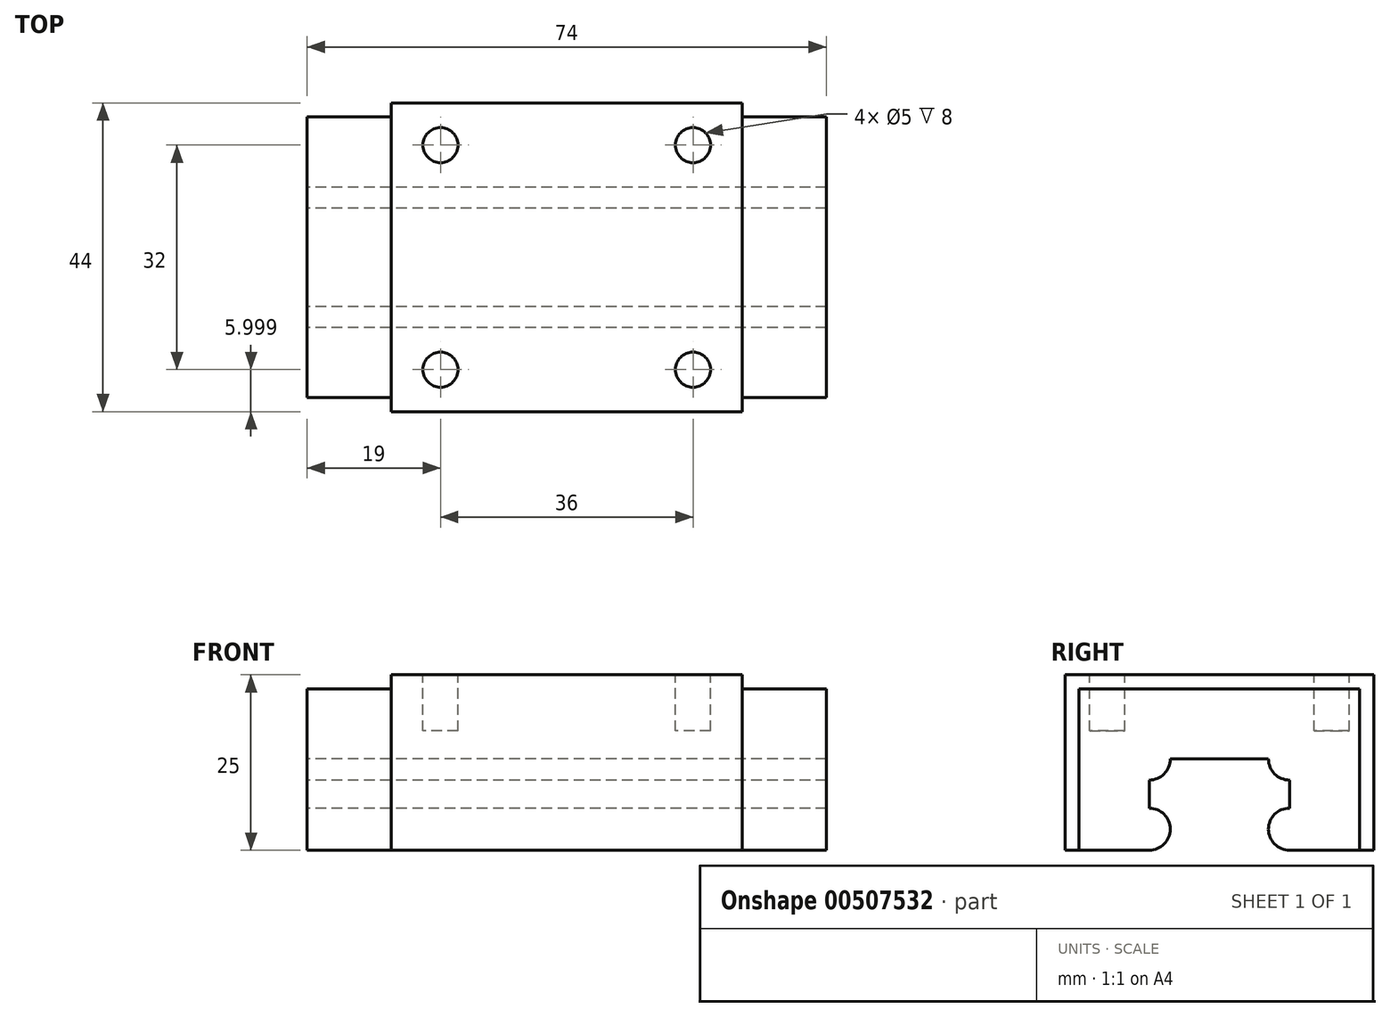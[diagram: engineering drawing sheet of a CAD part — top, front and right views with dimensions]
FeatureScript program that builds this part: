
annotation { "Feature Type Name" : "Feature", "Feature Type Description" : "" }
export const myFeature = defineFeature(function(context is Context, id is Id, definition is map)
    precondition{}
    {
        {
            var Q0;
            Q0=qCreatedBy(makeId("Right.planeOp"),FACE);
            var sketch = newSketch(context, id + "F0", { "sketchPlane" : qUnion([Q0])});
            skLineSegment(sketch, "E0", {"start": v(-26.04, 11) * mm, "end": v(-26.04, 15) * mm});
            skLineSegment(sketch, "E1", {"start": v(-23.04, 18) * mm, "end": v(-9.04, 18) * mm});
            skLineSegment(sketch, "E2", {"start": v(-6.04, 15) * mm, "end": v(-6.04, 11) * mm});
            skArc(sketch, "E3", {"start": v(-26.04, 5) * mm, "mid": v(-23.04, 8) * mm, "end": v(-26.04, 11) * mm});
            skArc(sketch, "E4", {"start": v(-6.04, 11) * mm, "mid": v(-9.04, 8) * mm, "end": v(-6.04, 5) * mm});
            skArc(sketch, "E5", {"start": v(-26.04, 15) * mm, "mid": v(-23.92, 15.88) * mm, "end": v(-23.04, 18) * mm});
            skArc(sketch, "E6", {"start": v(-9.04, 18) * mm, "mid": v(-8.16, 15.88) * mm, "end": v(-6.04, 15) * mm});
            skLineSegment(sketch, "E7", {"start": v(-38.04, 30) * mm, "end": v(5.96, 30) * mm});
            skLineSegment(sketch, "E8", {"start": v(-26.04, 5) * mm, "end": v(-38.04, 5) * mm});
            skLineSegment(sketch, "E9", {"start": v(-6.04, 5) * mm, "end": v(5.96, 5) * mm});
            skLineSegment(sketch, "E10", {"start": v(-38.04, 5) * mm, "end": v(-38.04, 30) * mm});
            skLineSegment(sketch, "E11", {"start": v(5.96, 5) * mm, "end": v(5.96, 30) * mm});
            skSolve(sketch);
        }
        {
            var Q0;
            Q0=qSketchRegion(id+"F0",true);
            extrude(context, id + "F1", {"entities" : qUnion([Q0]), "depth" : 74 * mm});
        }
        {
            var Q0;
            Q0=makeQuery(id+"F1.opExtrude","SWEPT_FACE",FACE,{"disambiguationData":[OSD([sQuery(id+"F0.wireOp",EDGE,"E7")])]});
            var sketch = newSketch(context, id + "F2", { "sketchPlane" : qUnion([Q0])});
            skLineSegment(sketch, "E12.bottom", {"start": v(74, -38.04) * mm, "end": v(62, -38.04) * mm});
            skLineSegment(sketch, "E12.top", {"start": v(74, 5.96) * mm, "end": v(62, 5.96) * mm});
            skLineSegment(sketch, "E12.left", {"start": v(74, -38.04) * mm, "end": v(74, 5.96) * mm});
            skLineSegment(sketch, "E12.right", {"start": v(62, -38.04) * mm, "end": v(62, 5.96) * mm});
            skLineSegment(sketch, "E13.bottom", {"start": v(0, -38.04) * mm, "end": v(12, -38.04) * mm});
            skLineSegment(sketch, "E13.top", {"start": v(0, 5.96) * mm, "end": v(12, 5.96) * mm});
            skLineSegment(sketch, "E13.left", {"start": v(0, -38.04) * mm, "end": v(0, 5.96) * mm});
            skLineSegment(sketch, "E13.right", {"start": v(12, -38.04) * mm, "end": v(12, 5.96) * mm});
            skSolve(sketch);
        }
        {
            var Q0;
            Q0=qSketchRegion(id+"F2",true);
            extrude(context, id + "F3", {"entities" : qUnion([Q0]), "operationType" : NewBodyOperationType.REMOVE, "oppositeDirection" : true, "depth" : 2 * mm});
        }
        {
            var Q0;
            Q0=makeQuery(id+"F1.opExtrude","SWEPT_FACE",FACE,{"disambiguationData":[OSD([sQuery(id+"F0.wireOp",EDGE,"E7")])]});
            var sketch = newSketch(context, id + "F4", { "sketchPlane" : qUnion([Q0])});
            skLineSegment(sketch, "E14.bottom", {"start": v(12, 5.96) * mm, "end": v(0, 5.96) * mm});
            skLineSegment(sketch, "E14.top", {"start": v(12, 3.96) * mm, "end": v(0, 3.96) * mm});
            skLineSegment(sketch, "E14.left", {"start": v(12, 5.96) * mm, "end": v(12, 3.96) * mm});
            skLineSegment(sketch, "E14.right", {"start": v(0, 5.96) * mm, "end": v(0, 3.96) * mm});
            skLineSegment(sketch, "E15.bottom", {"start": v(12, -38.04) * mm, "end": v(0, -38.04) * mm});
            skLineSegment(sketch, "E15.top", {"start": v(12, -36.04) * mm, "end": v(0, -36.04) * mm});
            skLineSegment(sketch, "E15.left", {"start": v(12, -38.04) * mm, "end": v(12, -36.04) * mm});
            skLineSegment(sketch, "E15.right", {"start": v(0, -38.04) * mm, "end": v(0, -36.04) * mm});
            skPoint(sketch, "E16.oppositeSnap0", {"position": v(6, -36.04) * mm});
            skLineSegment(sketch, "E16.bottom", {"start": v(62, -38.04) * mm, "end": v(74, -38.04) * mm});
            skLineSegment(sketch, "E16.top", {"start": v(62, -36.04) * mm, "end": v(74, -36.04) * mm});
            skLineSegment(sketch, "E16.left", {"start": v(62, -38.04) * mm, "end": v(62, -36.04) * mm});
            skLineSegment(sketch, "E16.right", {"start": v(74, -38.04) * mm, "end": v(74, -36.04) * mm});
            skLineSegment(sketch, "E17.bottom", {"start": v(62, 5.96) * mm, "end": v(74, 5.96) * mm});
            skLineSegment(sketch, "E17.top", {"start": v(62, 3.96) * mm, "end": v(74, 3.96) * mm});
            skLineSegment(sketch, "E17.left", {"start": v(62, 5.96) * mm, "end": v(62, 3.96) * mm});
            skLineSegment(sketch, "E17.right", {"start": v(74, 5.96) * mm, "end": v(74, 3.96) * mm});
            skSolve(sketch);
        }
        {
            var Q0;
            Q0=qSketchRegion(id+"F4",true);
            extrude(context, id + "F5", {"entities" : qUnion([Q0]), "operationType" : NewBodyOperationType.REMOVE, "oppositeDirection" : true, "depth" : 25 * mm});
        }
        {
            var Q0;
            Q0=makeQuery(id+"F1.opExtrude","SWEPT_FACE",FACE,{"disambiguationData":[OSD([sQuery(id+"F0.wireOp",EDGE,"E7")])]});
            var sketch = newSketch(context, id + "F6", { "sketchPlane" : qUnion([Q0])});
            skLineSegment(sketch, "E18.bottom", {"start": v(21.5, -32.04) * mm, "end": v(52.5, -32.04) * mm});
            skLineSegment(sketch, "E18.top", {"start": v(21.5, -0.04) * mm, "end": v(52.5, -0.04) * mm});
            skLineSegment(sketch, "E18.left", {"start": v(19, -29.54) * mm, "end": v(19, -2.54) * mm});
            skLineSegment(sketch, "E18.right", {"start": v(55, -29.54) * mm, "end": v(55, -2.54) * mm});
            skCircle(sketch, "E19", {"center": v(19, -0.04) * mm, "radius": 2.5 * mm});
            skCircle(sketch, "E20", {"center": v(55, -0.04) * mm, "radius": 2.5 * mm});
            skCircle(sketch, "E21", {"center": v(55, -32.04) * mm, "radius": 2.5 * mm});
            skCircle(sketch, "E22", {"center": v(19, -32.04) * mm, "radius": 2.5 * mm});
            skSolve(sketch);
        }
        {
            var Q0;
            {var subQ0=sQuery(id+"F6.wireOp",EDGE,"E19");var subQ1=makeQuery(id+"F6.imprint","INTERSECT",VERTEX,{"derivedFrom":[sQuery(id+"F6.wireOp",EDGE,"E18.top"),subQ0]});Q0=makeQuery(id+"F6.imprint","IMPRINT",FACE,{"disambiguationData":[TD([[makeQuery(id+"F6.imprint","IMPRINT",EDGE,{"disambiguationData":[TD([[subQ1,-1.0]])],"derivedFrom":subQ0}),1.0]])]});}
            var Q1;
            {var subQ0=sQuery(id+"F6.wireOp",EDGE,"E20");var subQ1=makeQuery(id+"F6.imprint","INTERSECT",VERTEX,{"derivedFrom":[sQuery(id+"F6.wireOp",EDGE,"E18.top"),subQ0]});Q1=makeQuery(id+"F6.imprint","IMPRINT",FACE,{"disambiguationData":[TD([[makeQuery(id+"F6.imprint","IMPRINT",EDGE,{"disambiguationData":[TD([[subQ1,-1.0]])],"derivedFrom":subQ0}),1.0]])]});}
            var Q2;
            {var subQ0=sQuery(id+"F6.wireOp",EDGE,"E21");var subQ1=makeQuery(id+"F6.imprint","INTERSECT",VERTEX,{"derivedFrom":[sQuery(id+"F6.wireOp",EDGE,"E18.bottom"),subQ0]});Q2=makeQuery(id+"F6.imprint","IMPRINT",FACE,{"disambiguationData":[TD([[makeQuery(id+"F6.imprint","IMPRINT",EDGE,{"disambiguationData":[TD([[subQ1,1.0]])],"derivedFrom":subQ0}),1.0]])]});}
            var Q3;
            {var subQ0=sQuery(id+"F6.wireOp",EDGE,"E22");var subQ1=makeQuery(id+"F6.imprint","INTERSECT",VERTEX,{"derivedFrom":[sQuery(id+"F6.wireOp",EDGE,"E18.bottom"),subQ0]});Q3=makeQuery(id+"F6.imprint","IMPRINT",FACE,{"disambiguationData":[TD([[makeQuery(id+"F6.imprint","IMPRINT",EDGE,{"disambiguationData":[TD([[subQ1,-1.0]])],"derivedFrom":subQ0}),1.0]])]});}
            extrude(context, id + "F7", {"entities" : qUnion([Q0, Q1, Q2, Q3]), "operationType" : NewBodyOperationType.REMOVE, "oppositeDirection" : true, "depth" : 8 * mm});
        }
    });
